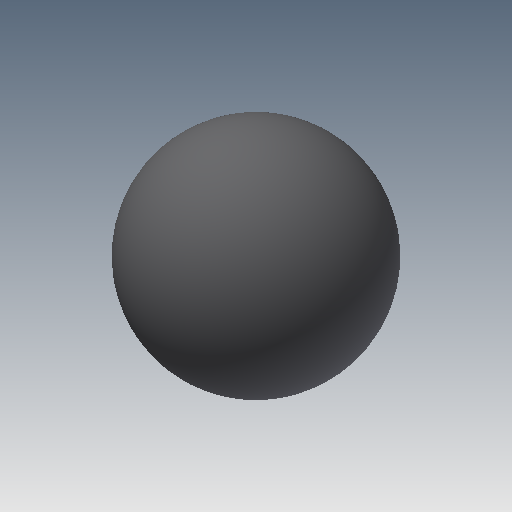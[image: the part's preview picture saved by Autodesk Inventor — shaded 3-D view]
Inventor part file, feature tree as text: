
AUTODESK INVENTOR PART (.ipt)
format: ipt  version: 2019.4 (Build 234330000, 330)  size: 138,240 bytes
history: native  units: mm
features: other x7, revolve x1, sketch x1
ambient origin geometry x8: Origin, YZ Plane, XZ Plane, XY Plane, X Axis, Y Axis, Z Axis, Center Point
bodies: Solid1 (feature_tree)
feature tree (9):
  revolve  "Revolution1"  [1 undecoded]
  other  "ip_st_1_XY"
  other  "ip_st_1_YZ"
  other  "ip_st_1_ZX"
  other  "ip_st_1_X"
  other  "ip_st_1_Y"
  other  "ip_st_1_Z"
  other  "ip_st_1_Center"
  sketch  "Sketch_1"  dims[d0=360.0deg]
note: 1 required parameter value undecoded (feature->parameter linkage not recoverable at this tier; creation-order binding heuristic only, values carry confidence <= 0.55)
